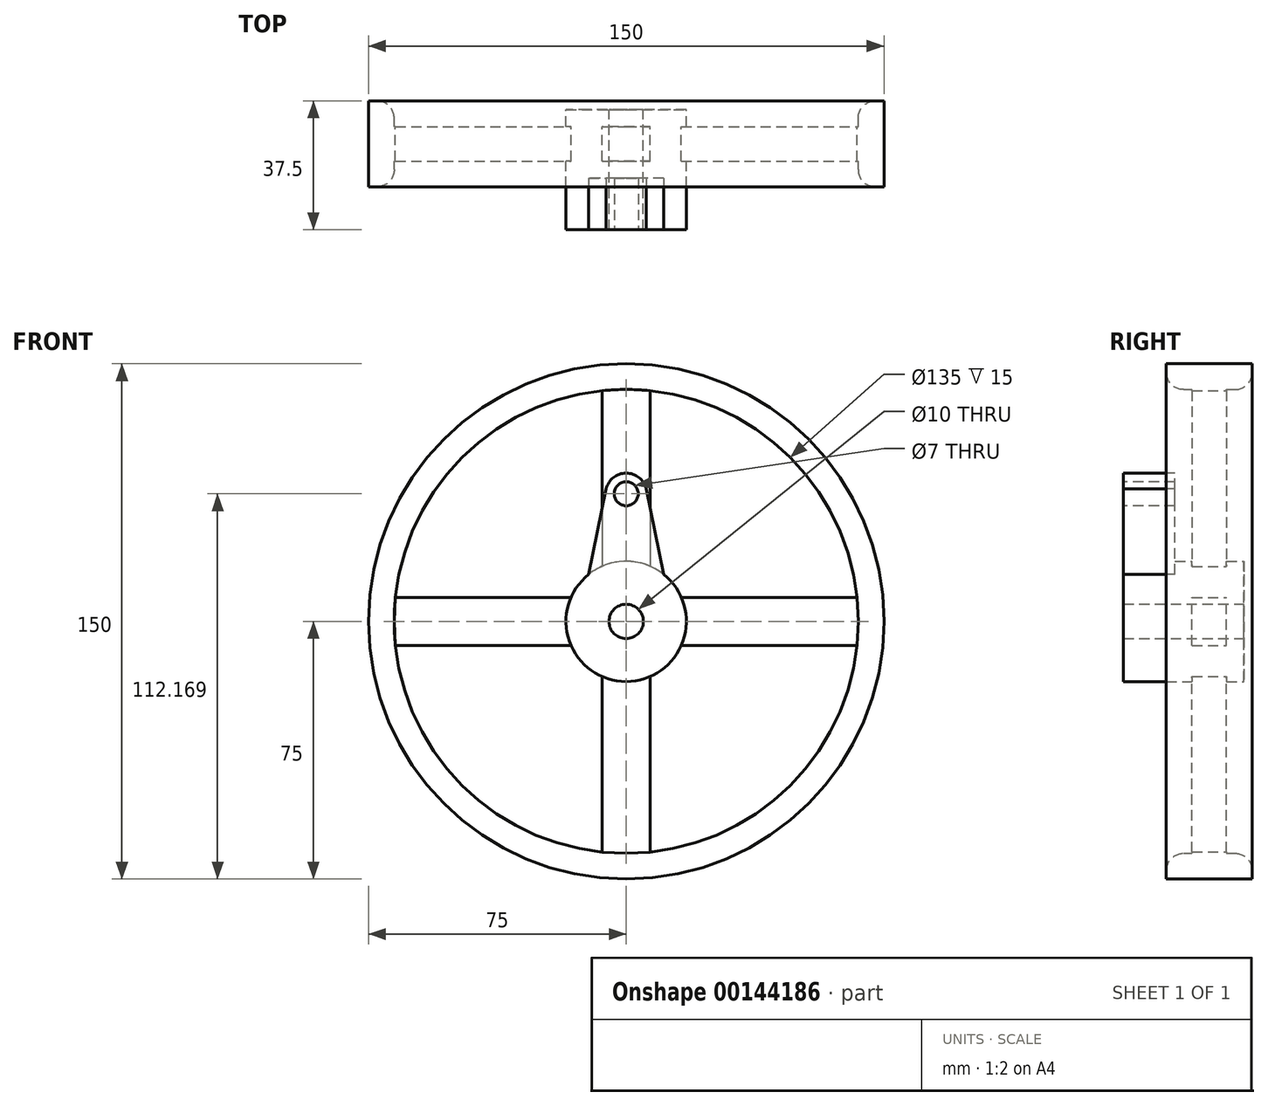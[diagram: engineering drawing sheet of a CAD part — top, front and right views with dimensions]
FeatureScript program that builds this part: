
annotation { "Feature Type Name" : "Feature", "Feature Type Description" : "" }
export const myFeature = defineFeature(function(context is Context, id is Id, definition is map)
    precondition{}
    {
        {
            var Q0;
            Q0=qCreatedBy(makeId("Front.planeOp"),FACE);
            var sketch = newSketch(context, id + "F0", { "sketchPlane" : qUnion([Q0])});
            skCircle(sketch, "E0", {"center": v(0, 0) * mm, "radius": 75 * mm});
            skCircle(sketch, "E1", {"center": v(0, 0) * mm, "radius": 5 * mm});
            skCircle(sketch, "E2", {"center": v(0, 0) * mm, "radius": 17.5 * mm});
            skCircle(sketch, "E3", {"center": v(0, 0) * mm, "radius": 67.5 * mm});
            skLineSegment(sketch, "E4", {"start": v(-104.76, 0) * mm, "end": v(135.02, 0) * mm, "construction": true});
            skLineSegment(sketch, "E5", {"start": v(0, 101.5) * mm, "end": v(0, -112.2) * mm, "construction": true});
            skLineSegment(sketch, "E6", {"start": v(-7, 67.14) * mm, "end": v(-7, 16.04) * mm});
            skLineSegment(sketch, "E7.MirrorCS", {"start": v(7, 67.14) * mm, "end": v(7, 16.04) * mm});
            skLineSegment(sketch, "E8.MirrorCS", {"start": v(104.76, 0) * mm, "end": v(-135.02, 0) * mm, "construction": true});
            skLineSegment(sketch, "E9.MirrorCS", {"start": v(-7, -67.14) * mm, "end": v(-7, -16.04) * mm});
            skLineSegment(sketch, "E10.MirrorCS", {"start": v(7, -67.14) * mm, "end": v(7, -16.04) * mm});
            skLineSegment(sketch, "E11", {"start": v(-67.14, -7) * mm, "end": v(-16.04, -7) * mm});
            skLineSegment(sketch, "E12.MirrorCS", {"start": v(-67.14, 7) * mm, "end": v(-16.04, 7) * mm});
            skLineSegment(sketch, "E13", {"start": v(16.04, 7) * mm, "end": v(67.14, 7) * mm});
            skLineSegment(sketch, "E14.MirrorCS", {"start": v(16.04, -7) * mm, "end": v(67.14, -7) * mm});
            skSolve(sketch);
        }
        {
            var Q0;
            Q0=makeQuery(id+"F0.imprint","IMPRINT",FACE,{"disambiguationData":[TD([[makeQuery(id+"F0.imprint","IMPRINT",EDGE,{"derivedFrom":sQuery(id+"F0.wireOp",EDGE,"E0")}),1.0]])]});
            extrude(context, id + "F1", {"entities" : qUnion([Q0]), "endBound" : BoundingType.SYMMETRIC, "depth" : 25 * mm});
        }
        {
            var Q0;
            Q0=makeQuery(id+"F0.imprint","IMPRINT",FACE,{"disambiguationData":[TD([[makeQuery(id+"F0.imprint","IMPRINT",EDGE,{"derivedFrom":sQuery(id+"F0.wireOp",EDGE,"E1")}),-1.0]])]});
            extrude(context, id + "F2", {"entities" : qUnion([Q0]), "endBound" : BoundingType.SYMMETRIC, "depth" : 20 * mm});
        }
        {
            var Q0;
            {var subQ0=sQuery(id+"F0.wireOp",EDGE,"E6");Q0=makeQuery(id+"F0.imprint","IMPRINT",FACE,{"disambiguationData":[TD([[makeQuery(id+"F0.imprint","IMPRINT",EDGE,{"derivedFrom":subQ0}),1.0]])]});}
            var Q1;
            {var subQ0=sQuery(id+"F0.wireOp",EDGE,"E13");Q1=makeQuery(id+"F0.imprint","IMPRINT",FACE,{"disambiguationData":[TD([[makeQuery(id+"F0.imprint","IMPRINT",EDGE,{"derivedFrom":subQ0}),-1.0]])]});}
            var Q2;
            {var subQ0=sQuery(id+"F0.wireOp",EDGE,"E10.MirrorCS");Q2=makeQuery(id+"F0.imprint","IMPRINT",FACE,{"disambiguationData":[TD([[makeQuery(id+"F0.imprint","IMPRINT",EDGE,{"derivedFrom":subQ0}),1.0]])]});}
            var Q3;
            {var subQ0=sQuery(id+"F0.wireOp",EDGE,"E12.MirrorCS");Q3=makeQuery(id+"F0.imprint","IMPRINT",FACE,{"disambiguationData":[TD([[makeQuery(id+"F0.imprint","IMPRINT",EDGE,{"derivedFrom":subQ0}),-1.0]])]});}
            extrude(context, id + "F3", {"entities" : qUnion([Q0, Q1, Q2, Q3]), "operationType" : NewBodyOperationType.ADD, "endBound" : BoundingType.SYMMETRIC, "depth" : 10 * mm});
        }
        {
            var Q0;
            Q0=makeQuery(id+"F2.opExtrude","CAP_FACE",FACE,{"disambiguationData":[OSD([sQuery(id+"F0.wireOp",EDGE,"E1"),sQuery(id+"F0.wireOp",EDGE,"E2")])],"isStart":false});
            var sketch = newSketch(context, id + "F4", { "sketchPlane" : qUnion([Q0])});
            skCircle(sketch, "E15", {"center": v(0, 0) * mm, "radius": 17.5 * mm});
            skSolve(sketch);
        }
        {
            var Q0;
            Q0=makeQuery(id+"F4.imprint","IMPRINT",FACE,{"disambiguationData":[TD([[makeQuery(id+"F4.imprint","IMPRINT",EDGE,{"derivedFrom":sQuery(id+"F4.wireOp",EDGE,"E15")}),1.0]])]});
            extrude(context, id + "F5", {"entities" : qUnion([Q0]), "operationType" : NewBodyOperationType.ADD, "depth" : 15 * mm});
        }
        {
            var Q0;
            Q0=makeQuery(id+"F5.opExtrude","CAP_FACE",FACE,{"disambiguationData":[OSD([sQuery(id+"F0.wireOp",EDGE,"E1"),sQuery(id+"F4.wireOp",EDGE,"E15")])],"isStart":false});
            var sketch = newSketch(context, id + "F6", { "sketchPlane" : qUnion([Q0])});
            skLineSegment(sketch, "E16", {"start": v(0, 60.45) * mm, "end": v(0, -40.67) * mm, "construction": true});
            skLineSegment(sketch, "E17", {"start": v(-10.88, 13.7) * mm, "end": v(-5.82, 38.62) * mm});
            skArc(sketch, "E18", {"start": v(-5.82, 38.62) * mm, "mid": v(-3.7, 41.9) * mm, "end": v(0, 43.17) * mm});
            skLineSegment(sketch, "E19.MirrorCS", {"start": v(10.88, 13.7) * mm, "end": v(5.82, 38.62) * mm});
            skArc(sketch, "E20.MirrorCS", {"start": v(5.82, 38.62) * mm, "mid": v(3.7, 41.9) * mm, "end": v(0, 43.17) * mm});
            skCircle(sketch, "E21", {"center": v(0, 37.17) * mm, "radius": 3.5 * mm});
            skSolve(sketch);
        }
        {
            var Q0;
            {var subQ1=sQuery(id+"F6.wireOp",EDGE,"E17");Q0=makeQuery(id+"F6.imprint","IMPRINT",FACE,{"disambiguationData":[TD([[makeQuery(id+"F6.imprint","IMPRINT",EDGE,{"derivedFrom":subQ1}),-1.0]])]});}
            extrude(context, id + "F7", {"entities" : qUnion([Q0]), "operationType" : NewBodyOperationType.ADD, "oppositeDirection" : true, "depth" : 15 * mm});
        }
        {
            var Q0;
            Q0=makeQuery(id+"F1.opExtrude","CAP_EDGE",EDGE,{"disambiguationData":[OSD([sQuery(id+"F0.wireOp",EDGE,"E3")])],"isStart":false});
            var Q1;
            Q1=makeQuery(id+"F1.opExtrude","CAP_EDGE",EDGE,{"disambiguationData":[OSD([sQuery(id+"F0.wireOp",EDGE,"E3")])],"isStart":true});
            fillet(context, id + "F8", {"entities" : qUnion([Q0, Q1]), "radius" : 5 * mm, "tangentPropagation" : true, "allowEdgeOverflow" : false});
        }
    });
